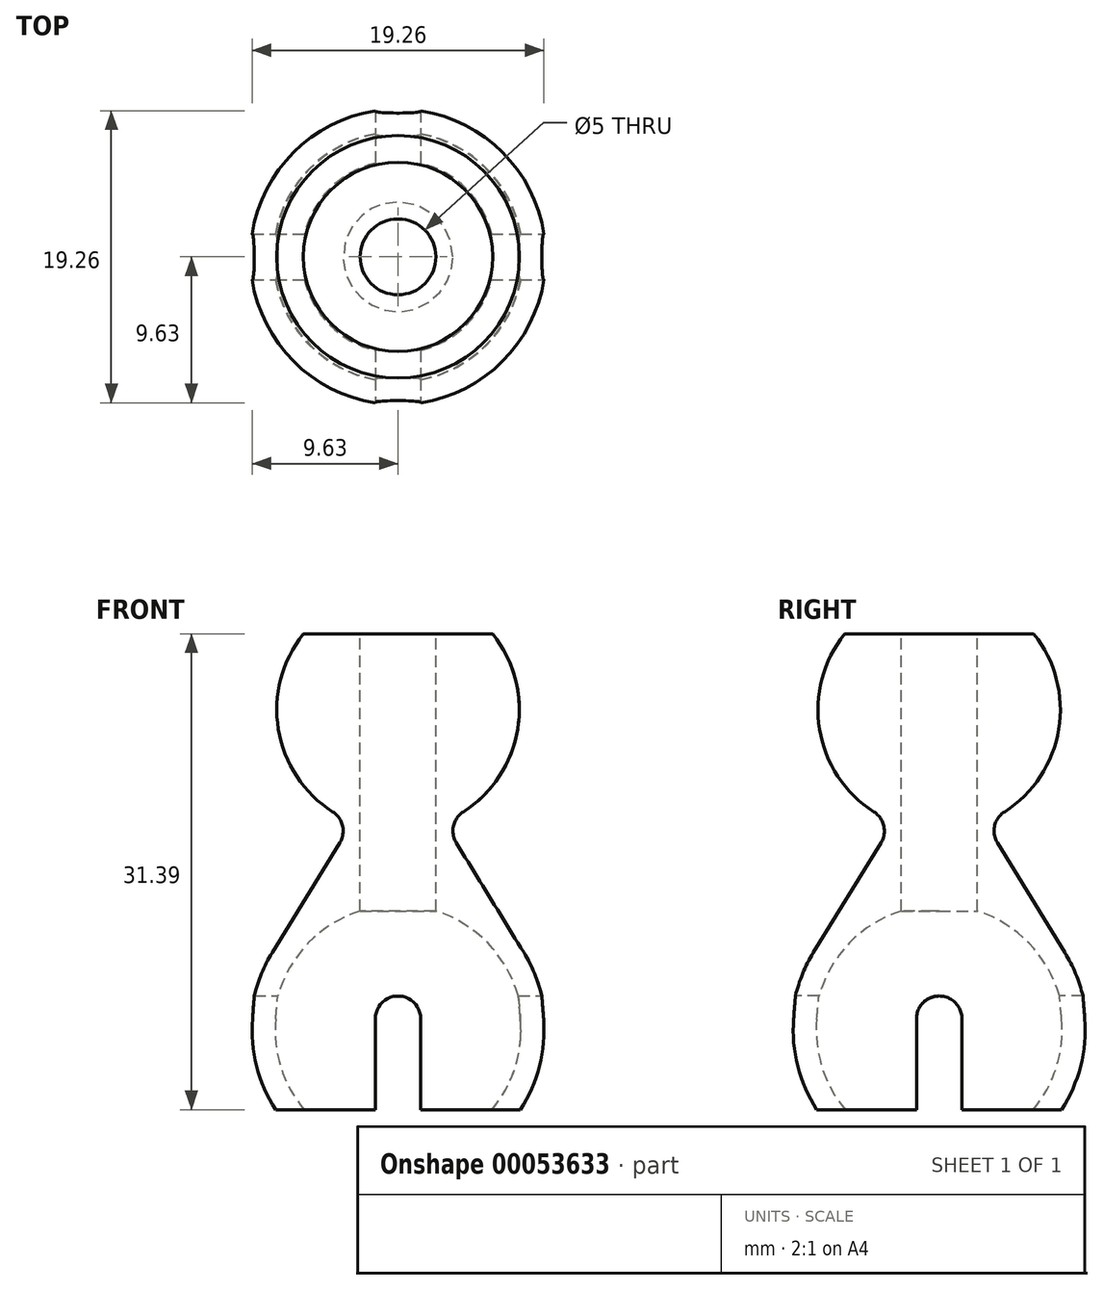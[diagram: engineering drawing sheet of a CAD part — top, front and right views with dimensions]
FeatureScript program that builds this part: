
annotation { "Feature Type Name" : "Feature", "Feature Type Description" : "" }
export const myFeature = defineFeature(function(context is Context, id is Id, definition is map)
    precondition{}
    {
        {
            var Q0;
            Q0=qCreatedBy(makeId("Front.planeOp"),FACE);
            var sketch = newSketch(context, id + "F0", { "sketchPlane" : qUnion([Q0])});
            skArc(sketch, "E0", {"start": v(4.31, -6.74) * mm, "mid": v(7.9, -1.3) * mm, "end": v(6.24, 5) * mm});
            skArc(sketch, "E1", {"start": v(6.36, -26.4) * mm, "mid": v(7.46, -17.62) * mm, "end": v(0, -12.9) * mm});
            skPoint(sketch, "E2.orphan", {"position": v(8, 0) * mm});
            skLineSegment(sketch, "E3", {"start": v(3.84, -8.79) * mm, "end": v(8.3, -16.03) * mm});
            skArc(sketch, "E4", {"start": v(8.22, -26.4) * mm, "mid": v(9.75, -21.22) * mm, "end": v(8.3, -16.03) * mm});
            skLineSegment(sketch, "E5", {"start": v(0, 5) * mm, "end": v(6.24, 5) * mm});
            skPoint(sketch, "E6.orphan", {"position": v(0, 8) * mm});
            skLineSegment(sketch, "E7", {"start": v(0, -12.9) * mm, "end": v(0, -8) * mm});
            skLineSegment(sketch, "E8", {"start": v(0, 5) * mm, "end": v(0, -8) * mm});
            skLineSegment(sketch, "E9", {"start": v(6.36, -26.4) * mm, "end": v(8.22, -26.4) * mm});
            skPoint(sketch, "E10.visualSharp", {"position": v(3, -7.42) * mm});
            skArc(sketch, "E10.filletArc", {"start": v(4.31, -6.74) * mm, "mid": v(3.66, -7.67) * mm, "end": v(3.84, -8.79) * mm});
            skLineSegment(sketch, "E11", {"start": v(0, -12.9) * mm, "end": v(0, -26.4) * mm, "construction": true});
            skSolve(sketch);
        }
        {
            var Q0;
            Q0 = qSketchRegion(id + "F0", true);
            var Q1;
            Q1=sQuery(id+"F0.wireOp",EDGE,"E11");
            revolve(context, id + "F1", {"entities" : qUnion([Q0]), "axis" : qUnion([Q1]), "revolveType" : RevolveType.FULL});
        }
        {
            var Q0;
            Q0=makeQuery(id+"F1.opRevolve","SWEPT_FACE",FACE,{"disambiguationData":[OSD([sQuery(id+"F0.wireOp",EDGE,"E5")])]});
            var sketch = newSketch(context, id + "F2", { "sketchPlane" : qUnion([Q0])});
            skCircle(sketch, "E12", {"center": v(0, 0) * mm, "radius": 2.5 * mm});
            skSolve(sketch);
        }
        {
            var Q0;
            Q0 = qSketchRegion(id + "F2", true);
            extrude(context, id + "F3", {"entities" : qUnion([Q0]), "operationType" : NewBodyOperationType.REMOVE, "endBound" : BoundingType.THROUGH_ALL, "oppositeDirection" : true, "depth" : 25 * mm});
        }
        {
            var Q0;
            Q0=qCreatedBy(makeId("Front.planeOp"),FACE);
            var sketch = newSketch(context, id + "F4", { "sketchPlane" : qUnion([Q0])});
            skLineSegment(sketch, "E13.top", {"start": v(-1.5, -26.4) * mm, "end": v(1.5, -26.4) * mm});
            skLineSegment(sketch, "E13.left", {"start": v(-1.5, -20.4) * mm, "end": v(-1.5, -26.4) * mm});
            skLineSegment(sketch, "E13.right", {"start": v(1.5, -20.4) * mm, "end": v(1.5, -26.4) * mm});
            skArc(sketch, "E14", {"start": v(1.5, -20.4) * mm, "mid": v(0, -18.9) * mm, "end": v(-1.5, -20.4) * mm});
            skSolve(sketch);
        }
        {
            var Q0;
            Q0 = qSketchRegion(id + "F4", true);
            extrude(context, id + "F5", {"entities" : qUnion([Q0]), "operationType" : NewBodyOperationType.REMOVE, "endBound" : BoundingType.SYMMETRIC, "oppositeDirection" : true, "depth" : 25 * mm});
        }
        {
            var Q0;
            Q0=qCreatedBy(makeId("Right.planeOp"),FACE);
            var sketch = newSketch(context, id + "F6", { "sketchPlane" : qUnion([Q0])});
            skLineSegment(sketch, "E15.top", {"start": v(-1.5, -26.4) * mm, "end": v(1.5, -26.4) * mm});
            skLineSegment(sketch, "E15.left", {"start": v(-1.5, -20.4) * mm, "end": v(-1.5, -26.4) * mm});
            skLineSegment(sketch, "E15.right", {"start": v(1.5, -20.4) * mm, "end": v(1.5, -26.4) * mm});
            skArc(sketch, "E16", {"start": v(1.5, -20.4) * mm, "mid": v(0, -18.9) * mm, "end": v(-1.5, -20.4) * mm});
            skSolve(sketch);
        }
        {
            var Q0;
            Q0 = qSketchRegion(id + "F6", true);
            extrude(context, id + "F7", {"entities" : qUnion([Q0]), "operationType" : NewBodyOperationType.REMOVE, "endBound" : BoundingType.SYMMETRIC, "oppositeDirection" : true, "depth" : 25 * mm});
        }
    });
